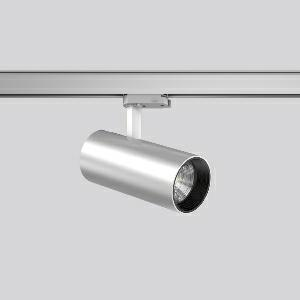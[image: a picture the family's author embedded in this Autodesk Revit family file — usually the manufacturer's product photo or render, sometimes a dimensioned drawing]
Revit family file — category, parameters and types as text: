
# Revit family: deecos_s_mini_742198_004_76_0b45
name_source: partatom
category: Lighting Fixtures
units: mm (PartAtom-declared; Revit-internal decimal feet)

## family parameters
Cut with Voids When Loaded = No
Host = Face
Light Source = No
Part Type = Normal
Room Calculation Point = No
Round Connector Dimension = Use Diameter
Shared = No

## types (1)
- DEECOS S mini (1 x LED Modul 930, 2250 lm, 3000)
    Apparent Load = 20 VA
    Approval mark = CE
    CIE Flux Codes = 99 100 100 100 100
    Color Rendering = 90
    Color Temperature = 3000
    Default Elevation = 1800 mm
    Description = Series: DEECOS S mini
LED surface-mounted projector in modern design with no visible cooling ribs. Housing: die-cast aluminium, powder-coated. Rotation range: 356°. Swivel range: 90°. Black plastic ring and recessed LED to prevent glare from the side. Optical assembly with lens made of plastic (polycarbonate) for the best homogeneous light distribution - can be changed without tools. Best colour rendering index Ra>90. With adapter for RZB 3-circuit DALI tracks. Suitable for Track on ceiling, Wall track. High quality converter without flickering and stroboscopic effect. The following accessories can be mounted without use of tools: interchangeable lenses, decorative glasses, honeycomb louvre, clear and frosted diffusers, white interchangeable plastic ring. 
Colour: silver
Diameter: 87 mm
Height: 214 mm
Lamp: LED
Socket: without socket
Colour temperature: 3000K
Colour rendering index (CRI): 92
System power: 20 W
Rated luminous flux: 2250 lm
Luminous efficiency: 113 lm/W
Control gear: Converter, dimmable, DALI
Protection class: I
Type of protection: IP 20
    Height = 214 mm
    Lamp = 1 x LED Modul 930
    Lamp Light Flux = 2250 lm
    Lamp count = 1
    Length = 87 mm
    Lifetime = 50000 h
    Luminous efficacy = 113 lm/W
    Manufacturer = RZB
    ModVariant = No
    Model = 742198.004.76
    Mounting Place = Ceiling
    Mounting Type = Rail mounted
    Number of Poles = 1
    OnlyDefault = Yes
    Power Factor = 1
    Product Name = DEECOS S mini
    Product group = Track mounted projectors
    ProductGroupID = 301
    Protection Class = Protection class I
    Protection Degree = IP 20
    RLX_Detail_Level = 1
    RLX_Emergency_Light_Flux = 0 lm
    RLX_Emergency_Type = 0
    RLX_Emergency_Type_DB = No
    RlxData = <blob elided: 37629 chars, md5=0fd1da6d>
    Socket = socket
    Standby Power = 0 W
    System Light Flux = 2250 lm
    System Power = 20 W
    Type Comments = Product without accessories
    Type Image = 741930.004.jpg
    URL = http://relux.com
    VarID = ---
    Voltage = 230 V
    Voltage Range = 220-240 V
    Weight = 0.00 kg
    Width = 0 mm  [stored 0 ft]

note: [stored X ft] marks values corroborated as IEEE doubles in the binary element streams (Revit-internal decimal feet)

## geometry (parser evidence)
native form markers: Blend x4, Sweep x11
no freeform markers — native parametric forms only
